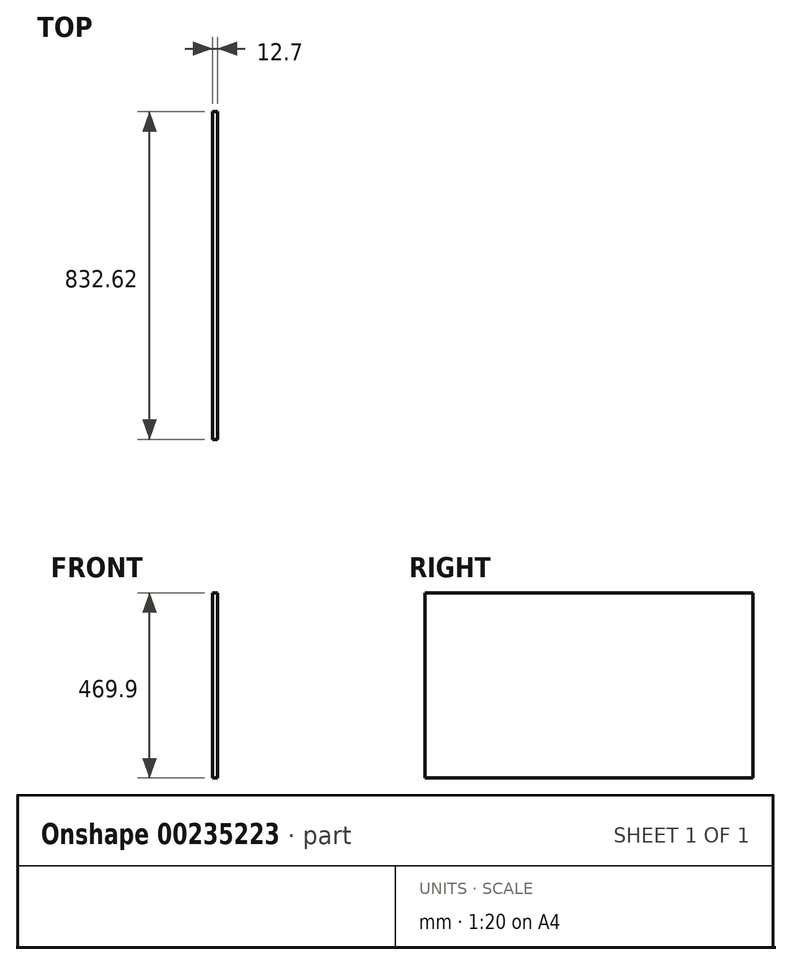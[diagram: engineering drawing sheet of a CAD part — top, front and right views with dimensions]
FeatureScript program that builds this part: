
annotation { "Feature Type Name" : "Feature", "Feature Type Description" : "" }
export const myFeature = defineFeature(function(context is Context, id is Id, definition is map)
    precondition{}
    {
        {
            var Q0;
            Q0=qCreatedBy(makeId("Right.planeOp"),FACE);
            var sketch = newSketch(context, id + "F0", { "sketchPlane" : qUnion([Q0])});
            skLineSegment(sketch, "E0.bottom", {"start": v(-416.3, 234.95) * mm, "end": v(416.3, 234.95) * mm});
            skLineSegment(sketch, "E0.top", {"start": v(-416.3, -234.95) * mm, "end": v(416.3, -234.95) * mm});
            skLineSegment(sketch, "E0.left", {"start": v(-416.3, 234.95) * mm, "end": v(-416.3, -234.95) * mm});
            skLineSegment(sketch, "E0.right", {"start": v(416.3, 234.95) * mm, "end": v(416.3, -234.95) * mm});
            skSolve(sketch);
        }
        {
            var Q0;
            Q0=makeQuery(id+"F0.imprint","IMPRINT",FACE,{"disambiguationData":[TD([[makeQuery(id+"F0.imprint","IMPRINT",EDGE,{"derivedFrom":sQuery(id+"F0.wireOp",EDGE,"E0.bottom")}),-1.0]])]});
            extrude(context, id + "F1", {"entities" : qUnion([Q0]), "depth" : 12.7 * mm});
        }
    });
